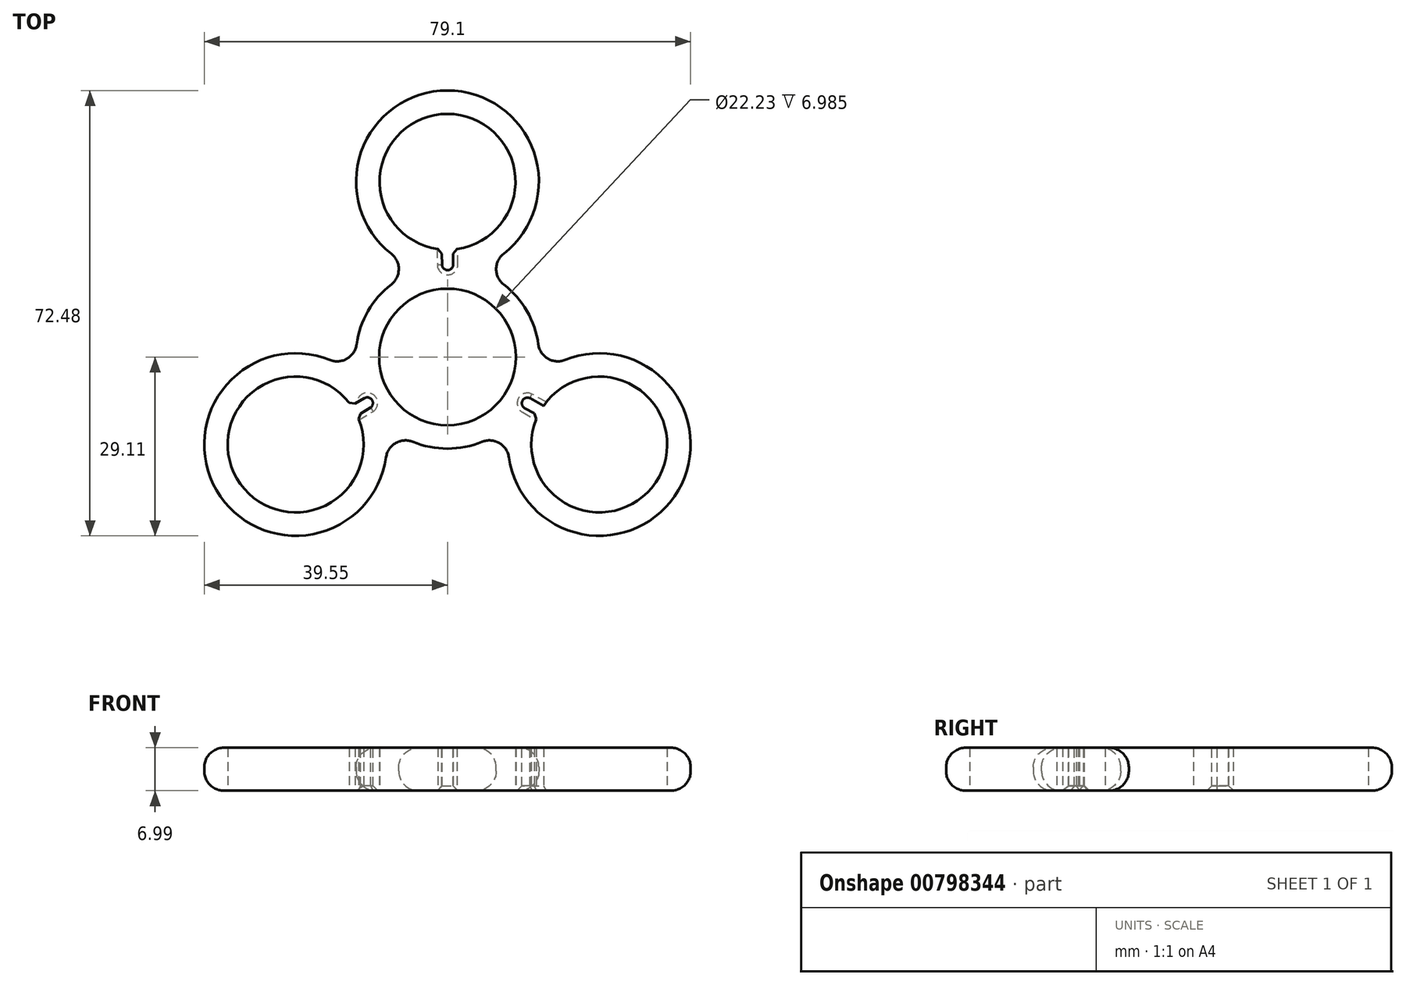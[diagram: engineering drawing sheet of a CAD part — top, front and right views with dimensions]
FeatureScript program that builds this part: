
annotation { "Feature Type Name" : "Feature", "Feature Type Description" : "" }
export const myFeature = defineFeature(function(context is Context, id is Id, definition is map)
    precondition{}
    {
        {
            var Q0;
            Q0=qCreatedBy(makeId("Top.planeOp"),FACE);
            var sketch = newSketch(context, id + "F0", { "sketchPlane" : qUnion([Q0])});
            skCircle(sketch, "E0", {"center": v(0, 0) * mm, "radius": 11.11 * mm});
            skCircle(sketch, "E1", {"center": v(0, 0) * mm, "radius": 14.92 * mm});
            skCircle(sketch, "E2", {"center": v(0, 28.51) * mm, "radius": 11.05 * mm});
            skCircle(sketch, "E3.0", {"center": v(0, 28.51) * mm, "radius": 14.86 * mm});
            skLineSegment(sketch, "E4", {"start": v(-5.64, 14.77) * mm, "end": v(-5.64, 13.81) * mm});
            skLineSegment(sketch, "E5.MirrorCS", {"start": v(5.64, 14.77) * mm, "end": v(5.64, 13.81) * mm});
            skCircle(sketch, "E6.1.0", {"center": v(-24.7, -14.26) * mm, "radius": 11.05 * mm});
            skCircle(sketch, "E6.1.1", {"center": v(-24.7, -14.26) * mm, "radius": 14.86 * mm});
            skLineSegment(sketch, "E6.1.2", {"start": v(-15.6, -2.5) * mm, "end": v(-14.79, -2.02) * mm});
            skLineSegment(sketch, "E6.1.3", {"start": v(-9.97, -12.27) * mm, "end": v(-9.14, -11.8) * mm});
            skCircle(sketch, "E6.2.0", {"center": v(24.7, -14.26) * mm, "radius": 11.05 * mm});
            skCircle(sketch, "E6.2.1", {"center": v(24.7, -14.26) * mm, "radius": 14.86 * mm});
            skLineSegment(sketch, "E6.2.2", {"start": v(9.97, -12.27) * mm, "end": v(9.14, -11.8) * mm});
            skLineSegment(sketch, "E6.2.3", {"start": v(15.6, -2.5) * mm, "end": v(14.79, -2.02) * mm});
            skLineSegment(sketch, "E7", {"start": v(0, 0) * mm, "end": v(0, 28.51) * mm, "construction": true});
            skSolve(sketch);
        }
        {
            var Q0;
            Q0=makeQuery(id+"F0.imprint","IMPRINT",FACE,{"disambiguationData":[TD([[makeQuery(id+"F0.imprint","IMPRINT",EDGE,{"derivedFrom":sQuery(id+"F0.wireOp",EDGE,"E0")}),-1.0]])]});
            extrude(context, id + "F1", {"entities" : qUnion([Q0]), "depth" : 7 * mm, "offsetDistance" : 25.4 * mm});
        }
        {
            var Q0;
            Q0=makeQuery(id+"F0.imprint","IMPRINT",FACE,{"disambiguationData":[TD([[makeQuery(id+"F0.imprint","IMPRINT",EDGE,{"derivedFrom":sQuery(id+"F0.wireOp",EDGE,"E6.2.0")}),-1.0]])]});
            var Q1;
            {var subQ0=sQuery(id+"F0.wireOp",EDGE,"E5.MirrorCS");Q1=makeQuery(id+"F0.imprint","IMPRINT",FACE,{"disambiguationData":[TD([[makeQuery(id+"F0.imprint","IMPRINT",EDGE,{"derivedFrom":subQ0}),1.0]])]});}
            var Q2;
            Q2=makeQuery(id+"F0.imprint","IMPRINT",FACE,{"disambiguationData":[TD([[makeQuery(id+"F0.imprint","IMPRINT",EDGE,{"derivedFrom":sQuery(id+"F0.wireOp",EDGE,"E2")}),-1.0]])]});
            var Q3;
            {var subQ0=sQuery(id+"F0.wireOp",EDGE,"E4");Q3=makeQuery(id+"F0.imprint","IMPRINT",FACE,{"disambiguationData":[TD([[makeQuery(id+"F0.imprint","IMPRINT",EDGE,{"derivedFrom":subQ0}),-1.0]])]});}
            var Q4;
            {var subQ0=sQuery(id+"F0.wireOp",EDGE,"E6.2.3");Q4=makeQuery(id+"F0.imprint","IMPRINT",FACE,{"disambiguationData":[TD([[makeQuery(id+"F0.imprint","IMPRINT",EDGE,{"derivedFrom":subQ0}),-1.0]])]});}
            var Q5;
            {var subQ0=sQuery(id+"F0.wireOp",EDGE,"E6.2.2");Q5=makeQuery(id+"F0.imprint","IMPRINT",FACE,{"disambiguationData":[TD([[makeQuery(id+"F0.imprint","IMPRINT",EDGE,{"derivedFrom":subQ0}),1.0]])]});}
            var Q6;
            Q6=makeQuery(id+"F0.imprint","IMPRINT",FACE,{"disambiguationData":[TD([[makeQuery(id+"F0.imprint","IMPRINT",EDGE,{"derivedFrom":sQuery(id+"F0.wireOp",EDGE,"E6.1.0")}),-1.0]])]});
            var Q7;
            {var subQ0=sQuery(id+"F0.wireOp",EDGE,"E6.1.3");Q7=makeQuery(id+"F0.imprint","IMPRINT",FACE,{"disambiguationData":[TD([[makeQuery(id+"F0.imprint","IMPRINT",EDGE,{"derivedFrom":subQ0}),-1.0]])]});}
            var Q8;
            Q8=makeQuery(id+"F0.imprint","IMPRINT",FACE,{"disambiguationData":[TD([[makeQuery(id+"F0.imprint","IMPRINT",EDGE,{"derivedFrom":sQuery(id+"F0.wireOp",EDGE,"E0")}),-1.0]])]});
            var Q9;
            {var subQ0=sQuery(id+"F0.wireOp",EDGE,"E6.1.2");Q9=makeQuery(id+"F0.imprint","IMPRINT",FACE,{"disambiguationData":[TD([[makeQuery(id+"F0.imprint","IMPRINT",EDGE,{"derivedFrom":subQ0}),1.0]])]});}
            var Q10;
            {var subQ0=sQuery(id+"F0.wireOp",EDGE,"E3.0");var subQ1=sQuery(id+"F0.wireOp",EDGE,"E1");var subQ2=makeQuery(id+"F0.imprint","INTERSECT",VERTEX,{"disambiguationData":[OD(0.0)],"derivedFrom":[subQ1,subQ0]});Q10=makeQuery(id+"F0.imprint","IMPRINT",FACE,{"disambiguationData":[TD([[makeQuery(id+"F0.imprint","IMPRINT",EDGE,{"disambiguationData":[TD([[subQ2,-1.0]])],"derivedFrom":subQ1}),1.0]])]});}
            var Q11;
            {var subQ0=sQuery(id+"F0.wireOp",EDGE,"E6.2.1");var subQ1=sQuery(id+"F0.wireOp",EDGE,"E1");var subQ2=makeQuery(id+"F0.imprint","INTERSECT",VERTEX,{"disambiguationData":[OD(0.0)],"derivedFrom":[subQ1,subQ0]});Q11=makeQuery(id+"F0.imprint","IMPRINT",FACE,{"disambiguationData":[TD([[makeQuery(id+"F0.imprint","IMPRINT",EDGE,{"disambiguationData":[TD([[subQ2,-1.0]])],"derivedFrom":subQ1}),1.0]])]});}
            var Q12;
            {var subQ0=sQuery(id+"F0.wireOp",EDGE,"E6.1.1");var subQ1=sQuery(id+"F0.wireOp",EDGE,"E1");var subQ2=makeQuery(id+"F0.imprint","INTERSECT",VERTEX,{"disambiguationData":[OD(0.0)],"derivedFrom":[subQ1,subQ0]});Q12=makeQuery(id+"F0.imprint","IMPRINT",FACE,{"disambiguationData":[TD([[makeQuery(id+"F0.imprint","IMPRINT",EDGE,{"disambiguationData":[TD([[subQ2,-1.0]])],"derivedFrom":subQ1}),1.0]])]});}
            extrude(context, id + "F2", {"entities" : qUnion([Q0, Q1, Q2, Q3, Q4, Q5, Q6, Q7, Q8, Q9, Q10, Q11, Q12]), "operationType" : NewBodyOperationType.ADD, "depth" : 7 * mm, "offsetDistance" : 25.4 * mm});
        }
        {
            var Q0;
            {var subQ0=sQuery(id+"F0.wireOp",EDGE,"E3.0");var subQ1=sQuery(id+"F0.wireOp",EDGE,"E1");var subQ2=makeQuery(id+"F0.imprint","INTERSECT",VERTEX,{"disambiguationData":[OD(1.0)],"derivedFrom":[subQ1,subQ0]});Q0=makeQuery(id+"F2.boolean.opBoolean","MERGE",EDGE,{"derivedFrom":[makeQuery(id+"F1.opExtrude","SWEPT_EDGE",EDGE,{"disambiguationData":[OSD([subQ1,subQ0]),TDD([subQ2])]}),makeQuery(id+"F2.opExtrude","SWEPT_EDGE",EDGE,{"disambiguationData":[OSD([subQ1,subQ0]),TDD([subQ2])]})]});}
            var Q1;
            {var subQ0=sQuery(id+"F0.wireOp",EDGE,"E3.0");var subQ1=sQuery(id+"F0.wireOp",EDGE,"E1");var subQ2=makeQuery(id+"F0.imprint","INTERSECT",VERTEX,{"disambiguationData":[OD(0.0)],"derivedFrom":[subQ1,subQ0]});Q1=makeQuery(id+"F2.boolean.opBoolean","MERGE",EDGE,{"derivedFrom":[makeQuery(id+"F1.opExtrude","SWEPT_EDGE",EDGE,{"disambiguationData":[OSD([subQ1,subQ0]),TDD([subQ2])]}),makeQuery(id+"F2.opExtrude","SWEPT_EDGE",EDGE,{"disambiguationData":[OSD([subQ1,subQ0]),TDD([subQ2])]})]});}
            var Q2;
            {var subQ0=sQuery(id+"F0.wireOp",EDGE,"E6.2.1");var subQ1=sQuery(id+"F0.wireOp",EDGE,"E1");var subQ2=makeQuery(id+"F0.imprint","INTERSECT",VERTEX,{"disambiguationData":[OD(1.0)],"derivedFrom":[subQ1,subQ0]});Q2=makeQuery(id+"F2.boolean.opBoolean","MERGE",EDGE,{"derivedFrom":[makeQuery(id+"F1.opExtrude","SWEPT_EDGE",EDGE,{"disambiguationData":[OSD([subQ1,subQ0]),TDD([subQ2])]}),makeQuery(id+"F2.opExtrude","SWEPT_EDGE",EDGE,{"disambiguationData":[OSD([subQ1,subQ0]),TDD([subQ2])]})]});}
            var Q3;
            {var subQ0=sQuery(id+"F0.wireOp",EDGE,"E6.2.1");var subQ1=sQuery(id+"F0.wireOp",EDGE,"E1");var subQ2=makeQuery(id+"F0.imprint","INTERSECT",VERTEX,{"disambiguationData":[OD(0.0)],"derivedFrom":[subQ1,subQ0]});Q3=makeQuery(id+"F2.boolean.opBoolean","MERGE",EDGE,{"derivedFrom":[makeQuery(id+"F1.opExtrude","SWEPT_EDGE",EDGE,{"disambiguationData":[OSD([subQ1,subQ0]),TDD([subQ2])]}),makeQuery(id+"F2.opExtrude","SWEPT_EDGE",EDGE,{"disambiguationData":[OSD([subQ1,subQ0]),TDD([subQ2])]})]});}
            var Q4;
            {var subQ0=sQuery(id+"F0.wireOp",EDGE,"E6.1.1");var subQ1=sQuery(id+"F0.wireOp",EDGE,"E1");var subQ2=makeQuery(id+"F0.imprint","INTERSECT",VERTEX,{"disambiguationData":[OD(1.0)],"derivedFrom":[subQ1,subQ0]});Q4=makeQuery(id+"F2.boolean.opBoolean","MERGE",EDGE,{"derivedFrom":[makeQuery(id+"F1.opExtrude","SWEPT_EDGE",EDGE,{"disambiguationData":[OSD([subQ1,subQ0]),TDD([subQ2])]}),makeQuery(id+"F2.opExtrude","SWEPT_EDGE",EDGE,{"disambiguationData":[OSD([subQ1,subQ0]),TDD([subQ2])]})]});}
            var Q5;
            {var subQ0=sQuery(id+"F0.wireOp",EDGE,"E6.1.1");var subQ1=sQuery(id+"F0.wireOp",EDGE,"E1");var subQ2=makeQuery(id+"F0.imprint","INTERSECT",VERTEX,{"disambiguationData":[OD(0.0)],"derivedFrom":[subQ1,subQ0]});Q5=makeQuery(id+"F2.boolean.opBoolean","MERGE",EDGE,{"derivedFrom":[makeQuery(id+"F1.opExtrude","SWEPT_EDGE",EDGE,{"disambiguationData":[OSD([subQ1,subQ0]),TDD([subQ2])]}),makeQuery(id+"F2.opExtrude","SWEPT_EDGE",EDGE,{"disambiguationData":[OSD([subQ1,subQ0]),TDD([subQ2])]})]});}
            fillet(context, id + "F3", {"entities" : qUnion([Q0, Q1, Q2, Q3, Q4, Q5]), "radius" : 3.17 * mm, "tangentPropagation" : true, "allowEdgeOverflow" : false});
        }
        {
            var Q0;
            {var subQ0=sQuery(id+"F0.wireOp",EDGE,"E6.1.3");var subQ1=sQuery(id+"F0.wireOp",EDGE,"E1");Q0=makeQuery(id+"F2.boolean.opBoolean","SPLIT",EDGE,{"disambiguationData":[TD([makeQuery(id+"F2.opExtrude","SWEPT_FACE",FACE,{"disambiguationData":[OSD([subQ0])]})])],"derivedFrom":makeQuery(id+"F1.opExtrude","CAP_EDGE",EDGE,{"disambiguationData":[OSD([subQ1])],"isStart":false})});}
            var Q1;
            Q1=makeQuery(id+"F2.opExtrude","CAP_EDGE",EDGE,{"disambiguationData":[OSD([sQuery(id+"F0.wireOp",EDGE,"E3.0")])],"isStart":true});
            var Q2;
            Q2=makeQuery(id+"F2.opExtrude","CAP_EDGE",EDGE,{"disambiguationData":[OSD([sQuery(id+"F0.wireOp",EDGE,"E6.2.1")])],"isStart":false});
            var Q3;
            Q3=makeQuery(id+"F2.opExtrude","CAP_EDGE",EDGE,{"disambiguationData":[OSD([sQuery(id+"F0.wireOp",EDGE,"E6.2.1")])],"isStart":true});
            var Q4;
            {var subQ0=sQuery(id+"F0.wireOp",EDGE,"E1");var subQ1=makeQuery(id+"F0.imprint","INTERSECT",VERTEX,{"derivedFrom":[subQ0,sQuery(id+"F0.wireOp",EDGE,"E5.MirrorCS")]});var subQ2=makeQuery(id+"F0.imprint","INTERSECT",VERTEX,{"derivedFrom":[subQ0,sQuery(id+"F0.wireOp",EDGE,"E6.2.3")]});Q4=makeQuery(id+"F1.opExtrude","CAP_EDGE",EDGE,{"disambiguationData":[OSD([subQ0]),TDD([makeQuery(id+"F0.imprint","IMPRINT",EDGE,{"disambiguationData":[TD([[subQ1,-1.0]])],"derivedFrom":subQ0}),makeQuery(id+"F0.imprint","IMPRINT",EDGE,{"disambiguationData":[TD([[subQ2,1.0]])],"derivedFrom":subQ0}),makeQuery(id+"F0.imprint","IMPRINT",EDGE,{"disambiguationData":[TD([[subQ1,1.0]])],"derivedFrom":subQ0})])],"isStart":true});}
            var Q5;
            {var subQ0=sQuery(id+"F0.wireOp",EDGE,"E6.2.1");var subQ1=sQuery(id+"F0.wireOp",EDGE,"E6.1.1");var subQ2=sQuery(id+"F0.wireOp",EDGE,"E5.MirrorCS");var subQ3=sQuery(id+"F0.wireOp",EDGE,"E3.0");var subQ4=sQuery(id+"F0.wireOp",EDGE,"E1");var subQ5=sQuery(id+"F0.wireOp",EDGE,"E0");Q5=makeQuery(id+"F3.opFillet","BLEND_EDGE",EDGE,{"blendedFrom":[makeQuery(id+"F2.opExtrude","SWEPT_EDGE",EDGE,{"disambiguationData":[OSD([subQ4,subQ2])]}),makeQuery(id+"F2.boolean.opBoolean","MERGE",FACE,{"derivedFrom":[makeQuery(id+"F1.opExtrude","CAP_FACE",FACE,{"disambiguationData":[OSD([subQ5,subQ4,subQ3,subQ1,subQ0])],"isStart":true}),makeQuery(id+"F2.opExtrude","CAP_FACE",FACE,{"disambiguationData":[OSD([subQ5,subQ4,sQuery(id+"F0.wireOp",EDGE,"E2"),subQ3,sQuery(id+"F0.wireOp",EDGE,"E4"),subQ2,sQuery(id+"F0.wireOp",EDGE,"E6.1.0"),subQ1,sQuery(id+"F0.wireOp",EDGE,"E6.1.2"),sQuery(id+"F0.wireOp",EDGE,"E6.2.0"),subQ0,sQuery(id+"F0.wireOp",EDGE,"E6.2.2")])],"isStart":true})]})],"blendedInto":[makeQuery(id+"F2.boolean.opBoolean","MERGE",FACE,{"derivedFrom":[makeQuery(id+"F1.opExtrude","CAP_FACE",FACE,{"disambiguationData":[OSD([subQ5,subQ4,subQ3,subQ1,subQ0])],"isStart":true}),makeQuery(id+"F2.opExtrude","CAP_FACE",FACE,{"disambiguationData":[OSD([subQ5,subQ4,sQuery(id+"F0.wireOp",EDGE,"E2"),subQ3,sQuery(id+"F0.wireOp",EDGE,"E4"),subQ2,sQuery(id+"F0.wireOp",EDGE,"E6.1.0"),subQ1,sQuery(id+"F0.wireOp",EDGE,"E6.1.2"),sQuery(id+"F0.wireOp",EDGE,"E6.2.0"),subQ0,sQuery(id+"F0.wireOp",EDGE,"E6.2.2")])],"isStart":true})]})]});}
            var Q6;
            {var subQ0=sQuery(id+"F0.wireOp",EDGE,"E6.2.1");var subQ1=sQuery(id+"F0.wireOp",EDGE,"E6.1.1");var subQ2=sQuery(id+"F0.wireOp",EDGE,"E5.MirrorCS");var subQ3=sQuery(id+"F0.wireOp",EDGE,"E3.0");var subQ4=sQuery(id+"F0.wireOp",EDGE,"E1");var subQ5=sQuery(id+"F0.wireOp",EDGE,"E0");Q6=makeQuery(id+"F3.opFillet","BLEND_EDGE",EDGE,{"blendedFrom":[makeQuery(id+"F2.opExtrude","SWEPT_EDGE",EDGE,{"disambiguationData":[OSD([subQ3,subQ2])]}),makeQuery(id+"F2.boolean.opBoolean","MERGE",FACE,{"derivedFrom":[makeQuery(id+"F1.opExtrude","CAP_FACE",FACE,{"disambiguationData":[OSD([subQ5,subQ4,subQ3,subQ1,subQ0])],"isStart":true}),makeQuery(id+"F2.opExtrude","CAP_FACE",FACE,{"disambiguationData":[OSD([subQ5,subQ4,sQuery(id+"F0.wireOp",EDGE,"E2"),subQ3,sQuery(id+"F0.wireOp",EDGE,"E4"),subQ2,sQuery(id+"F0.wireOp",EDGE,"E6.1.0"),subQ1,sQuery(id+"F0.wireOp",EDGE,"E6.1.2"),sQuery(id+"F0.wireOp",EDGE,"E6.2.0"),subQ0,sQuery(id+"F0.wireOp",EDGE,"E6.2.2")])],"isStart":true})]})],"blendedInto":[makeQuery(id+"F2.boolean.opBoolean","MERGE",FACE,{"derivedFrom":[makeQuery(id+"F1.opExtrude","CAP_FACE",FACE,{"disambiguationData":[OSD([subQ5,subQ4,subQ3,subQ1,subQ0])],"isStart":true}),makeQuery(id+"F2.opExtrude","CAP_FACE",FACE,{"disambiguationData":[OSD([subQ5,subQ4,sQuery(id+"F0.wireOp",EDGE,"E2"),subQ3,sQuery(id+"F0.wireOp",EDGE,"E4"),subQ2,sQuery(id+"F0.wireOp",EDGE,"E6.1.0"),subQ1,sQuery(id+"F0.wireOp",EDGE,"E6.1.2"),sQuery(id+"F0.wireOp",EDGE,"E6.2.0"),subQ0,sQuery(id+"F0.wireOp",EDGE,"E6.2.2")])],"isStart":true})]})]});}
            var Q7;
            {var subQ0=sQuery(id+"F0.wireOp",EDGE,"E6.2.1");var subQ1=sQuery(id+"F0.wireOp",EDGE,"E6.1.1");var subQ2=sQuery(id+"F0.wireOp",EDGE,"E5.MirrorCS");var subQ3=sQuery(id+"F0.wireOp",EDGE,"E3.0");var subQ4=sQuery(id+"F0.wireOp",EDGE,"E1");var subQ5=sQuery(id+"F0.wireOp",EDGE,"E0");Q7=makeQuery(id+"F3.opFillet","BLEND_EDGE",EDGE,{"blendedFrom":[makeQuery(id+"F2.opExtrude","SWEPT_EDGE",EDGE,{"disambiguationData":[OSD([subQ4,subQ2])]}),makeQuery(id+"F2.boolean.opBoolean","MERGE",FACE,{"derivedFrom":[makeQuery(id+"F1.opExtrude","CAP_FACE",FACE,{"disambiguationData":[OSD([subQ5,subQ4,subQ3,subQ1,subQ0])],"isStart":false}),makeQuery(id+"F2.opExtrude","CAP_FACE",FACE,{"disambiguationData":[OSD([subQ5,subQ4,sQuery(id+"F0.wireOp",EDGE,"E2"),subQ3,sQuery(id+"F0.wireOp",EDGE,"E4"),subQ2,sQuery(id+"F0.wireOp",EDGE,"E6.1.0"),subQ1,sQuery(id+"F0.wireOp",EDGE,"E6.1.2"),sQuery(id+"F0.wireOp",EDGE,"E6.2.0"),subQ0,sQuery(id+"F0.wireOp",EDGE,"E6.2.2")])],"isStart":false})]})],"blendedInto":[makeQuery(id+"F2.boolean.opBoolean","MERGE",FACE,{"derivedFrom":[makeQuery(id+"F1.opExtrude","CAP_FACE",FACE,{"disambiguationData":[OSD([subQ5,subQ4,subQ3,subQ1,subQ0])],"isStart":false}),makeQuery(id+"F2.opExtrude","CAP_FACE",FACE,{"disambiguationData":[OSD([subQ5,subQ4,sQuery(id+"F0.wireOp",EDGE,"E2"),subQ3,sQuery(id+"F0.wireOp",EDGE,"E4"),subQ2,sQuery(id+"F0.wireOp",EDGE,"E6.1.0"),subQ1,sQuery(id+"F0.wireOp",EDGE,"E6.1.2"),sQuery(id+"F0.wireOp",EDGE,"E6.2.0"),subQ0,sQuery(id+"F0.wireOp",EDGE,"E6.2.2")])],"isStart":false})]})]});}
            var Q8;
            {var subQ0=sQuery(id+"F0.wireOp",EDGE,"E6.2.1");var subQ1=sQuery(id+"F0.wireOp",EDGE,"E6.1.1");var subQ2=sQuery(id+"F0.wireOp",EDGE,"E5.MirrorCS");var subQ3=sQuery(id+"F0.wireOp",EDGE,"E3.0");var subQ4=sQuery(id+"F0.wireOp",EDGE,"E1");var subQ5=sQuery(id+"F0.wireOp",EDGE,"E0");Q8=makeQuery(id+"F3.opFillet","BLEND_EDGE",EDGE,{"blendedFrom":[makeQuery(id+"F2.opExtrude","SWEPT_EDGE",EDGE,{"disambiguationData":[OSD([subQ3,subQ2])]}),makeQuery(id+"F2.boolean.opBoolean","MERGE",FACE,{"derivedFrom":[makeQuery(id+"F1.opExtrude","CAP_FACE",FACE,{"disambiguationData":[OSD([subQ5,subQ4,subQ3,subQ1,subQ0])],"isStart":false}),makeQuery(id+"F2.opExtrude","CAP_FACE",FACE,{"disambiguationData":[OSD([subQ5,subQ4,sQuery(id+"F0.wireOp",EDGE,"E2"),subQ3,sQuery(id+"F0.wireOp",EDGE,"E4"),subQ2,sQuery(id+"F0.wireOp",EDGE,"E6.1.0"),subQ1,sQuery(id+"F0.wireOp",EDGE,"E6.1.2"),sQuery(id+"F0.wireOp",EDGE,"E6.2.0"),subQ0,sQuery(id+"F0.wireOp",EDGE,"E6.2.2")])],"isStart":false})]})],"blendedInto":[makeQuery(id+"F2.boolean.opBoolean","MERGE",FACE,{"derivedFrom":[makeQuery(id+"F1.opExtrude","CAP_FACE",FACE,{"disambiguationData":[OSD([subQ5,subQ4,subQ3,subQ1,subQ0])],"isStart":false}),makeQuery(id+"F2.opExtrude","CAP_FACE",FACE,{"disambiguationData":[OSD([subQ5,subQ4,sQuery(id+"F0.wireOp",EDGE,"E2"),subQ3,sQuery(id+"F0.wireOp",EDGE,"E4"),subQ2,sQuery(id+"F0.wireOp",EDGE,"E6.1.0"),subQ1,sQuery(id+"F0.wireOp",EDGE,"E6.1.2"),sQuery(id+"F0.wireOp",EDGE,"E6.2.0"),subQ0,sQuery(id+"F0.wireOp",EDGE,"E6.2.2")])],"isStart":false})]})]});}
            var Q9;
            Q9=makeQuery(id+"F2.opExtrude","SWEPT_FACE",FACE,{"disambiguationData":[OSD([sQuery(id+"F0.wireOp",EDGE,"E3.0")])]});
            var Q10;
            {var subQ0=sQuery(id+"F0.wireOp",EDGE,"E6.2.2");var subQ1=sQuery(id+"F0.wireOp",EDGE,"E6.2.1");var subQ2=sQuery(id+"F0.wireOp",EDGE,"E6.1.1");var subQ3=sQuery(id+"F0.wireOp",EDGE,"E3.0");var subQ4=sQuery(id+"F0.wireOp",EDGE,"E1");var subQ5=sQuery(id+"F0.wireOp",EDGE,"E0");Q10=makeQuery(id+"F3.opFillet","BLEND_EDGE",EDGE,{"blendedFrom":[makeQuery(id+"F2.opExtrude","SWEPT_EDGE",EDGE,{"disambiguationData":[OSD([subQ4,subQ0])]}),makeQuery(id+"F2.boolean.opBoolean","MERGE",FACE,{"derivedFrom":[makeQuery(id+"F1.opExtrude","CAP_FACE",FACE,{"disambiguationData":[OSD([subQ5,subQ4,subQ3,subQ2,subQ1])],"isStart":false}),makeQuery(id+"F2.opExtrude","CAP_FACE",FACE,{"disambiguationData":[OSD([subQ5,subQ4,sQuery(id+"F0.wireOp",EDGE,"E2"),subQ3,sQuery(id+"F0.wireOp",EDGE,"E4"),sQuery(id+"F0.wireOp",EDGE,"E5.MirrorCS"),sQuery(id+"F0.wireOp",EDGE,"E6.1.0"),subQ2,sQuery(id+"F0.wireOp",EDGE,"E6.1.2"),sQuery(id+"F0.wireOp",EDGE,"E6.2.0"),subQ1,subQ0])],"isStart":false})]})],"blendedInto":[makeQuery(id+"F2.boolean.opBoolean","MERGE",FACE,{"derivedFrom":[makeQuery(id+"F1.opExtrude","CAP_FACE",FACE,{"disambiguationData":[OSD([subQ5,subQ4,subQ3,subQ2,subQ1])],"isStart":false}),makeQuery(id+"F2.opExtrude","CAP_FACE",FACE,{"disambiguationData":[OSD([subQ5,subQ4,sQuery(id+"F0.wireOp",EDGE,"E2"),subQ3,sQuery(id+"F0.wireOp",EDGE,"E4"),sQuery(id+"F0.wireOp",EDGE,"E5.MirrorCS"),sQuery(id+"F0.wireOp",EDGE,"E6.1.0"),subQ2,sQuery(id+"F0.wireOp",EDGE,"E6.1.2"),sQuery(id+"F0.wireOp",EDGE,"E6.2.0"),subQ1,subQ0])],"isStart":false})]})]});}
            var Q11;
            {var subQ0=sQuery(id+"F0.wireOp",EDGE,"E6.2.2");var subQ1=sQuery(id+"F0.wireOp",EDGE,"E6.2.1");var subQ2=sQuery(id+"F0.wireOp",EDGE,"E6.1.1");var subQ3=sQuery(id+"F0.wireOp",EDGE,"E3.0");var subQ4=sQuery(id+"F0.wireOp",EDGE,"E1");var subQ5=sQuery(id+"F0.wireOp",EDGE,"E0");Q11=makeQuery(id+"F3.opFillet","BLEND_EDGE",EDGE,{"blendedFrom":[makeQuery(id+"F2.opExtrude","SWEPT_EDGE",EDGE,{"disambiguationData":[OSD([subQ1,subQ0])]}),makeQuery(id+"F2.boolean.opBoolean","MERGE",FACE,{"derivedFrom":[makeQuery(id+"F1.opExtrude","CAP_FACE",FACE,{"disambiguationData":[OSD([subQ5,subQ4,subQ3,subQ2,subQ1])],"isStart":false}),makeQuery(id+"F2.opExtrude","CAP_FACE",FACE,{"disambiguationData":[OSD([subQ5,subQ4,sQuery(id+"F0.wireOp",EDGE,"E2"),subQ3,sQuery(id+"F0.wireOp",EDGE,"E4"),sQuery(id+"F0.wireOp",EDGE,"E5.MirrorCS"),sQuery(id+"F0.wireOp",EDGE,"E6.1.0"),subQ2,sQuery(id+"F0.wireOp",EDGE,"E6.1.2"),sQuery(id+"F0.wireOp",EDGE,"E6.2.0"),subQ1,subQ0])],"isStart":false})]})],"blendedInto":[makeQuery(id+"F2.boolean.opBoolean","MERGE",FACE,{"derivedFrom":[makeQuery(id+"F1.opExtrude","CAP_FACE",FACE,{"disambiguationData":[OSD([subQ5,subQ4,subQ3,subQ2,subQ1])],"isStart":false}),makeQuery(id+"F2.opExtrude","CAP_FACE",FACE,{"disambiguationData":[OSD([subQ5,subQ4,sQuery(id+"F0.wireOp",EDGE,"E2"),subQ3,sQuery(id+"F0.wireOp",EDGE,"E4"),sQuery(id+"F0.wireOp",EDGE,"E5.MirrorCS"),sQuery(id+"F0.wireOp",EDGE,"E6.1.0"),subQ2,sQuery(id+"F0.wireOp",EDGE,"E6.1.2"),sQuery(id+"F0.wireOp",EDGE,"E6.2.0"),subQ1,subQ0])],"isStart":false})]})]});}
            var Q12;
            {var subQ0=sQuery(id+"F0.wireOp",EDGE,"E6.2.1");var subQ1=sQuery(id+"F0.wireOp",EDGE,"E6.1.1");var subQ2=sQuery(id+"F0.wireOp",EDGE,"E3.0");var subQ3=sQuery(id+"F0.wireOp",EDGE,"E1");var subQ4=sQuery(id+"F0.wireOp",EDGE,"E0");Q12=makeQuery(id+"F3.opFillet","BLEND_EDGE",EDGE,{"blendedFrom":[makeQuery(id+"F2.boolean.opBoolean","MERGE",EDGE,{"derivedFrom":[makeQuery(id+"F1.opExtrude","SWEPT_EDGE",EDGE,{"disambiguationData":[OSD([subQ3,subQ0]),TDD([makeQuery(id+"F0.imprint","INTERSECT",VERTEX,{"disambiguationData":[OD(1.0)],"derivedFrom":[subQ3,subQ0]})])]}),makeQuery(id+"F2.opExtrude","SWEPT_EDGE",EDGE,{"disambiguationData":[OSD([subQ3,subQ0])]})]}),makeQuery(id+"F2.boolean.opBoolean","MERGE",FACE,{"derivedFrom":[makeQuery(id+"F1.opExtrude","CAP_FACE",FACE,{"disambiguationData":[OSD([subQ4,subQ3,subQ2,subQ1,subQ0])],"isStart":false}),makeQuery(id+"F2.opExtrude","CAP_FACE",FACE,{"disambiguationData":[OSD([subQ4,subQ3,sQuery(id+"F0.wireOp",EDGE,"E2"),subQ2,sQuery(id+"F0.wireOp",EDGE,"E4"),sQuery(id+"F0.wireOp",EDGE,"E5.MirrorCS"),sQuery(id+"F0.wireOp",EDGE,"E6.1.0"),subQ1,sQuery(id+"F0.wireOp",EDGE,"E6.1.2"),sQuery(id+"F0.wireOp",EDGE,"E6.2.0"),subQ0,sQuery(id+"F0.wireOp",EDGE,"E6.2.2")])],"isStart":false})]})],"blendedInto":[makeQuery(id+"F2.boolean.opBoolean","MERGE",FACE,{"derivedFrom":[makeQuery(id+"F1.opExtrude","CAP_FACE",FACE,{"disambiguationData":[OSD([subQ4,subQ3,subQ2,subQ1,subQ0])],"isStart":false}),makeQuery(id+"F2.opExtrude","CAP_FACE",FACE,{"disambiguationData":[OSD([subQ4,subQ3,sQuery(id+"F0.wireOp",EDGE,"E2"),subQ2,sQuery(id+"F0.wireOp",EDGE,"E4"),sQuery(id+"F0.wireOp",EDGE,"E5.MirrorCS"),sQuery(id+"F0.wireOp",EDGE,"E6.1.0"),subQ1,sQuery(id+"F0.wireOp",EDGE,"E6.1.2"),sQuery(id+"F0.wireOp",EDGE,"E6.2.0"),subQ0,sQuery(id+"F0.wireOp",EDGE,"E6.2.2")])],"isStart":false})]})]});}
            var Q13;
            {var subQ0=sQuery(id+"F0.wireOp",EDGE,"E6.2.1");var subQ1=sQuery(id+"F0.wireOp",EDGE,"E6.1.1");var subQ2=sQuery(id+"F0.wireOp",EDGE,"E3.0");var subQ3=sQuery(id+"F0.wireOp",EDGE,"E1");var subQ4=sQuery(id+"F0.wireOp",EDGE,"E0");Q13=makeQuery(id+"F3.opFillet","BLEND_EDGE",EDGE,{"blendedFrom":[makeQuery(id+"F2.boolean.opBoolean","MERGE",EDGE,{"derivedFrom":[makeQuery(id+"F1.opExtrude","SWEPT_EDGE",EDGE,{"disambiguationData":[OSD([subQ3,subQ1]),TDD([makeQuery(id+"F0.imprint","INTERSECT",VERTEX,{"disambiguationData":[OD(1.0)],"derivedFrom":[subQ3,subQ1]})])]}),makeQuery(id+"F2.opExtrude","SWEPT_EDGE",EDGE,{"disambiguationData":[OSD([subQ3,subQ1])]})]}),makeQuery(id+"F2.boolean.opBoolean","MERGE",FACE,{"derivedFrom":[makeQuery(id+"F1.opExtrude","CAP_FACE",FACE,{"disambiguationData":[OSD([subQ4,subQ3,subQ2,subQ1,subQ0])],"isStart":false}),makeQuery(id+"F2.opExtrude","CAP_FACE",FACE,{"disambiguationData":[OSD([subQ4,subQ3,sQuery(id+"F0.wireOp",EDGE,"E2"),subQ2,sQuery(id+"F0.wireOp",EDGE,"E4"),sQuery(id+"F0.wireOp",EDGE,"E5.MirrorCS"),sQuery(id+"F0.wireOp",EDGE,"E6.1.0"),subQ1,sQuery(id+"F0.wireOp",EDGE,"E6.1.2"),sQuery(id+"F0.wireOp",EDGE,"E6.2.0"),subQ0,sQuery(id+"F0.wireOp",EDGE,"E6.2.2")])],"isStart":false})]})],"blendedInto":[makeQuery(id+"F2.boolean.opBoolean","MERGE",FACE,{"derivedFrom":[makeQuery(id+"F1.opExtrude","CAP_FACE",FACE,{"disambiguationData":[OSD([subQ4,subQ3,subQ2,subQ1,subQ0])],"isStart":false}),makeQuery(id+"F2.opExtrude","CAP_FACE",FACE,{"disambiguationData":[OSD([subQ4,subQ3,sQuery(id+"F0.wireOp",EDGE,"E2"),subQ2,sQuery(id+"F0.wireOp",EDGE,"E4"),sQuery(id+"F0.wireOp",EDGE,"E5.MirrorCS"),sQuery(id+"F0.wireOp",EDGE,"E6.1.0"),subQ1,sQuery(id+"F0.wireOp",EDGE,"E6.1.2"),sQuery(id+"F0.wireOp",EDGE,"E6.2.0"),subQ0,sQuery(id+"F0.wireOp",EDGE,"E6.2.2")])],"isStart":false})]})]});}
            var Q14;
            Q14=makeQuery(id+"F2.opExtrude","CAP_EDGE",EDGE,{"disambiguationData":[OSD([sQuery(id+"F0.wireOp",EDGE,"E6.1.1")])],"isStart":false});
            var Q15;
            {var subQ0=sQuery(id+"F0.wireOp",EDGE,"E6.2.1");var subQ1=sQuery(id+"F0.wireOp",EDGE,"E6.1.2");var subQ2=sQuery(id+"F0.wireOp",EDGE,"E6.1.1");var subQ3=sQuery(id+"F0.wireOp",EDGE,"E3.0");var subQ4=sQuery(id+"F0.wireOp",EDGE,"E1");var subQ5=sQuery(id+"F0.wireOp",EDGE,"E0");Q15=makeQuery(id+"F3.opFillet","BLEND_EDGE",EDGE,{"blendedFrom":[makeQuery(id+"F2.opExtrude","SWEPT_EDGE",EDGE,{"disambiguationData":[OSD([subQ4,subQ1])]}),makeQuery(id+"F2.boolean.opBoolean","MERGE",FACE,{"derivedFrom":[makeQuery(id+"F1.opExtrude","CAP_FACE",FACE,{"disambiguationData":[OSD([subQ5,subQ4,subQ3,subQ2,subQ0])],"isStart":false}),makeQuery(id+"F2.opExtrude","CAP_FACE",FACE,{"disambiguationData":[OSD([subQ5,subQ4,sQuery(id+"F0.wireOp",EDGE,"E2"),subQ3,sQuery(id+"F0.wireOp",EDGE,"E4"),sQuery(id+"F0.wireOp",EDGE,"E5.MirrorCS"),sQuery(id+"F0.wireOp",EDGE,"E6.1.0"),subQ2,subQ1,sQuery(id+"F0.wireOp",EDGE,"E6.2.0"),subQ0,sQuery(id+"F0.wireOp",EDGE,"E6.2.2")])],"isStart":false})]})],"blendedInto":[makeQuery(id+"F2.boolean.opBoolean","MERGE",FACE,{"derivedFrom":[makeQuery(id+"F1.opExtrude","CAP_FACE",FACE,{"disambiguationData":[OSD([subQ5,subQ4,subQ3,subQ2,subQ0])],"isStart":false}),makeQuery(id+"F2.opExtrude","CAP_FACE",FACE,{"disambiguationData":[OSD([subQ5,subQ4,sQuery(id+"F0.wireOp",EDGE,"E2"),subQ3,sQuery(id+"F0.wireOp",EDGE,"E4"),sQuery(id+"F0.wireOp",EDGE,"E5.MirrorCS"),sQuery(id+"F0.wireOp",EDGE,"E6.1.0"),subQ2,subQ1,sQuery(id+"F0.wireOp",EDGE,"E6.2.0"),subQ0,sQuery(id+"F0.wireOp",EDGE,"E6.2.2")])],"isStart":false})]})]});}
            var Q16;
            {var subQ0=sQuery(id+"F0.wireOp",EDGE,"E6.2.1");var subQ1=sQuery(id+"F0.wireOp",EDGE,"E6.1.2");var subQ2=sQuery(id+"F0.wireOp",EDGE,"E6.1.1");var subQ3=sQuery(id+"F0.wireOp",EDGE,"E3.0");var subQ4=sQuery(id+"F0.wireOp",EDGE,"E1");var subQ5=sQuery(id+"F0.wireOp",EDGE,"E0");Q16=makeQuery(id+"F3.opFillet","BLEND_EDGE",EDGE,{"blendedFrom":[makeQuery(id+"F2.opExtrude","SWEPT_EDGE",EDGE,{"disambiguationData":[OSD([subQ2,subQ1])]}),makeQuery(id+"F2.boolean.opBoolean","MERGE",FACE,{"derivedFrom":[makeQuery(id+"F1.opExtrude","CAP_FACE",FACE,{"disambiguationData":[OSD([subQ5,subQ4,subQ3,subQ2,subQ0])],"isStart":false}),makeQuery(id+"F2.opExtrude","CAP_FACE",FACE,{"disambiguationData":[OSD([subQ5,subQ4,sQuery(id+"F0.wireOp",EDGE,"E2"),subQ3,sQuery(id+"F0.wireOp",EDGE,"E4"),sQuery(id+"F0.wireOp",EDGE,"E5.MirrorCS"),sQuery(id+"F0.wireOp",EDGE,"E6.1.0"),subQ2,subQ1,sQuery(id+"F0.wireOp",EDGE,"E6.2.0"),subQ0,sQuery(id+"F0.wireOp",EDGE,"E6.2.2")])],"isStart":false})]})],"blendedInto":[makeQuery(id+"F2.boolean.opBoolean","MERGE",FACE,{"derivedFrom":[makeQuery(id+"F1.opExtrude","CAP_FACE",FACE,{"disambiguationData":[OSD([subQ5,subQ4,subQ3,subQ2,subQ0])],"isStart":false}),makeQuery(id+"F2.opExtrude","CAP_FACE",FACE,{"disambiguationData":[OSD([subQ5,subQ4,sQuery(id+"F0.wireOp",EDGE,"E2"),subQ3,sQuery(id+"F0.wireOp",EDGE,"E4"),sQuery(id+"F0.wireOp",EDGE,"E5.MirrorCS"),sQuery(id+"F0.wireOp",EDGE,"E6.1.0"),subQ2,subQ1,sQuery(id+"F0.wireOp",EDGE,"E6.2.0"),subQ0,sQuery(id+"F0.wireOp",EDGE,"E6.2.2")])],"isStart":false})]})]});}
            var Q17;
            {var subQ0=sQuery(id+"F0.wireOp",EDGE,"E6.2.1");var subQ1=sQuery(id+"F0.wireOp",EDGE,"E6.1.1");var subQ2=sQuery(id+"F0.wireOp",EDGE,"E4");var subQ3=sQuery(id+"F0.wireOp",EDGE,"E3.0");var subQ4=sQuery(id+"F0.wireOp",EDGE,"E1");var subQ5=sQuery(id+"F0.wireOp",EDGE,"E0");Q17=makeQuery(id+"F3.opFillet","BLEND_EDGE",EDGE,{"blendedFrom":[makeQuery(id+"F2.opExtrude","SWEPT_EDGE",EDGE,{"disambiguationData":[OSD([subQ3,subQ2])]}),makeQuery(id+"F2.boolean.opBoolean","MERGE",FACE,{"derivedFrom":[makeQuery(id+"F1.opExtrude","CAP_FACE",FACE,{"disambiguationData":[OSD([subQ5,subQ4,subQ3,subQ1,subQ0])],"isStart":false}),makeQuery(id+"F2.opExtrude","CAP_FACE",FACE,{"disambiguationData":[OSD([subQ5,subQ4,sQuery(id+"F0.wireOp",EDGE,"E2"),subQ3,subQ2,sQuery(id+"F0.wireOp",EDGE,"E5.MirrorCS"),sQuery(id+"F0.wireOp",EDGE,"E6.1.0"),subQ1,sQuery(id+"F0.wireOp",EDGE,"E6.1.2"),sQuery(id+"F0.wireOp",EDGE,"E6.2.0"),subQ0,sQuery(id+"F0.wireOp",EDGE,"E6.2.2")])],"isStart":false})]})],"blendedInto":[makeQuery(id+"F2.boolean.opBoolean","MERGE",FACE,{"derivedFrom":[makeQuery(id+"F1.opExtrude","CAP_FACE",FACE,{"disambiguationData":[OSD([subQ5,subQ4,subQ3,subQ1,subQ0])],"isStart":false}),makeQuery(id+"F2.opExtrude","CAP_FACE",FACE,{"disambiguationData":[OSD([subQ5,subQ4,sQuery(id+"F0.wireOp",EDGE,"E2"),subQ3,subQ2,sQuery(id+"F0.wireOp",EDGE,"E5.MirrorCS"),sQuery(id+"F0.wireOp",EDGE,"E6.1.0"),subQ1,sQuery(id+"F0.wireOp",EDGE,"E6.1.2"),sQuery(id+"F0.wireOp",EDGE,"E6.2.0"),subQ0,sQuery(id+"F0.wireOp",EDGE,"E6.2.2")])],"isStart":false})]})]});}
            var Q18;
            {var subQ0=sQuery(id+"F0.wireOp",EDGE,"E6.2.1");var subQ1=sQuery(id+"F0.wireOp",EDGE,"E6.1.1");var subQ2=sQuery(id+"F0.wireOp",EDGE,"E4");var subQ3=sQuery(id+"F0.wireOp",EDGE,"E3.0");var subQ4=sQuery(id+"F0.wireOp",EDGE,"E1");var subQ5=sQuery(id+"F0.wireOp",EDGE,"E0");Q18=makeQuery(id+"F3.opFillet","BLEND_EDGE",EDGE,{"blendedFrom":[makeQuery(id+"F2.opExtrude","SWEPT_EDGE",EDGE,{"disambiguationData":[OSD([subQ4,subQ2])]}),makeQuery(id+"F2.boolean.opBoolean","MERGE",FACE,{"derivedFrom":[makeQuery(id+"F1.opExtrude","CAP_FACE",FACE,{"disambiguationData":[OSD([subQ5,subQ4,subQ3,subQ1,subQ0])],"isStart":false}),makeQuery(id+"F2.opExtrude","CAP_FACE",FACE,{"disambiguationData":[OSD([subQ5,subQ4,sQuery(id+"F0.wireOp",EDGE,"E2"),subQ3,subQ2,sQuery(id+"F0.wireOp",EDGE,"E5.MirrorCS"),sQuery(id+"F0.wireOp",EDGE,"E6.1.0"),subQ1,sQuery(id+"F0.wireOp",EDGE,"E6.1.2"),sQuery(id+"F0.wireOp",EDGE,"E6.2.0"),subQ0,sQuery(id+"F0.wireOp",EDGE,"E6.2.2")])],"isStart":false})]})],"blendedInto":[makeQuery(id+"F2.boolean.opBoolean","MERGE",FACE,{"derivedFrom":[makeQuery(id+"F1.opExtrude","CAP_FACE",FACE,{"disambiguationData":[OSD([subQ5,subQ4,subQ3,subQ1,subQ0])],"isStart":false}),makeQuery(id+"F2.opExtrude","CAP_FACE",FACE,{"disambiguationData":[OSD([subQ5,subQ4,sQuery(id+"F0.wireOp",EDGE,"E2"),subQ3,subQ2,sQuery(id+"F0.wireOp",EDGE,"E5.MirrorCS"),sQuery(id+"F0.wireOp",EDGE,"E6.1.0"),subQ1,sQuery(id+"F0.wireOp",EDGE,"E6.1.2"),sQuery(id+"F0.wireOp",EDGE,"E6.2.0"),subQ0,sQuery(id+"F0.wireOp",EDGE,"E6.2.2")])],"isStart":false})]})]});}
            fillet(context, id + "F4", {"entities" : qUnion([Q0, Q1, Q2, Q3, Q4, Q5, Q6, Q7, Q8, Q9, Q10, Q11, Q12, Q13, Q14, Q15, Q16, Q17, Q18]), "radius" : 3.17 * mm, "tangentPropagation" : true, "allowEdgeOverflow" : false});
        }
        {
            var Q0;
            {var subQ0=sQuery(id+"F0.wireOp",EDGE,"E1");Q0=makeQuery(id+"F2.boolean.opBoolean","MERGE",FACE,{"derivedFrom":[makeQuery(id+"F1.opExtrude","CAP_FACE",FACE,{"disambiguationData":[OSD([sQuery(id+"F0.wireOp",EDGE,"E0"),subQ0])],"isStart":false}),makeQuery(id+"F2.opExtrude","CAP_FACE",FACE,{"disambiguationData":[OSD([subQ0,sQuery(id+"F0.wireOp",EDGE,"E2"),sQuery(id+"F0.wireOp",EDGE,"E3.0"),sQuery(id+"F0.wireOp",EDGE,"E4"),sQuery(id+"F0.wireOp",EDGE,"E5.MirrorCS")])],"isStart":false}),makeQuery(id+"F2.opExtrude","CAP_FACE",FACE,{"disambiguationData":[OSD([subQ0,sQuery(id+"F0.wireOp",EDGE,"E6.1.0"),sQuery(id+"F0.wireOp",EDGE,"E6.1.1"),sQuery(id+"F0.wireOp",EDGE,"E6.1.2"),sQuery(id+"F0.wireOp",EDGE,"E6.1.3")])],"isStart":false}),makeQuery(id+"F2.opExtrude","CAP_FACE",FACE,{"disambiguationData":[OSD([subQ0,sQuery(id+"F0.wireOp",EDGE,"E6.2.0"),sQuery(id+"F0.wireOp",EDGE,"E6.2.1"),sQuery(id+"F0.wireOp",EDGE,"E6.2.2"),sQuery(id+"F0.wireOp",EDGE,"E6.2.3")])],"isStart":false})]});}
            var sketch = newSketch(context, id + "F5", { "sketchPlane" : qUnion([Q0])});
            skLineSegment(sketch, "E8.left", {"start": v(0.94, 15.05) * mm, "end": v(0.89, 19.22) * mm});
            skLineSegment(sketch, "E8.right", {"start": v(-0.89, 14.96) * mm, "end": v(-0.94, 19.13) * mm});
            skPoint(sketch, "E8.middle", {"position": v(0, 17.09) * mm});
            skArc(sketch, "E9", {"start": v(0.89, 19.22) * mm, "mid": v(-0.07, 20.12) * mm, "end": v(-0.94, 19.13) * mm});
            skArc(sketch, "E10", {"start": v(0.94, 15.05) * mm, "mid": v(0.07, 14.12) * mm, "end": v(-0.89, 14.96) * mm});
            skLineSegment(sketch, "E11.1.0", {"start": v(-13.5, -6.71) * mm, "end": v(-17.09, -8.84) * mm});
            skArc(sketch, "E11.1.1", {"start": v(-17.09, -8.84) * mm, "mid": v(-17.4, -10.12) * mm, "end": v(-16.1, -10.38) * mm});
            skLineSegment(sketch, "E11.1.2", {"start": v(-12.5, -8.25) * mm, "end": v(-16.1, -10.38) * mm});
            skArc(sketch, "E11.1.3", {"start": v(-13.5, -6.71) * mm, "mid": v(-12.27, -7) * mm, "end": v(-12.5, -8.25) * mm});
            skLineSegment(sketch, "E11.2.0", {"start": v(12.56, -8.34) * mm, "end": v(16.2, -10.38) * mm});
            skArc(sketch, "E11.2.1", {"start": v(16.2, -10.38) * mm, "mid": v(17.46, -10) * mm, "end": v(17.04, -8.75) * mm});
            skLineSegment(sketch, "E11.2.2", {"start": v(13.4, -6.71) * mm, "end": v(17.04, -8.75) * mm});
            skArc(sketch, "E11.2.3", {"start": v(12.56, -8.34) * mm, "mid": v(12.2, -7.13) * mm, "end": v(13.4, -6.71) * mm});
            skPoint(sketch, "E11.center", {"position": v(0, 0) * mm});
            skSolve(sketch);
        }
        {
            var Q0;
            Q0=makeQuery(id+"F5.imprint","IMPRINT",FACE,{"disambiguationData":[TD([[makeQuery(id+"F5.imprint","IMPRINT",EDGE,{"derivedFrom":sQuery(id+"F5.wireOp",EDGE,"E8.left")}),1.0]])]});
            var Q1;
            Q1=makeQuery(id+"F5.imprint","IMPRINT",FACE,{"disambiguationData":[TD([[makeQuery(id+"F5.imprint","IMPRINT",EDGE,{"derivedFrom":sQuery(id+"F5.wireOp",EDGE,"E11.1.0")}),1.0]])]});
            var Q2;
            Q2=makeQuery(id+"F5.imprint","IMPRINT",FACE,{"disambiguationData":[TD([[makeQuery(id+"F5.imprint","IMPRINT",EDGE,{"derivedFrom":sQuery(id+"F5.wireOp",EDGE,"E11.2.0")}),1.0]])]});
            extrude(context, id + "F6", {"entities" : qUnion([Q0, Q1, Q2]), "operationType" : NewBodyOperationType.REMOVE, "endBound" : BoundingType.THROUGH_ALL, "oppositeDirection" : true, "depth" : 25.4 * mm, "offsetDistance" : 25.4 * mm});
        }
        {
            var Q0;
            Q0=makeQuery(id+"F6.boolean.opBoolean","COPY",EDGE,{"derivedFrom":makeQuery(id+"F6.opExtrude","CAP_EDGE",EDGE,{"disambiguationData":[OSD([sQuery(id+"F5.wireOp",EDGE,"E11.1.2")])],"isStart":true})});
            var Q1;
            Q1=makeQuery(id+"F6.boolean.opBoolean","COPY",EDGE,{"derivedFrom":makeQuery(id+"F6.opExtrude","CAP_EDGE",EDGE,{"disambiguationData":[OSD([sQuery(id+"F5.wireOp",EDGE,"E11.1.1")])],"isStart":true})});
            var Q2;
            Q2=makeQuery(id+"F6.boolean.opBoolean","COPY",EDGE,{"derivedFrom":makeQuery(id+"F6.opExtrude","CAP_EDGE",EDGE,{"disambiguationData":[OSD([sQuery(id+"F5.wireOp",EDGE,"E11.1.0")])],"isStart":true})});
            var Q3;
            Q3=makeQuery(id+"F6.boolean.opBoolean","COPY",EDGE,{"derivedFrom":makeQuery(id+"F6.opExtrude","CAP_EDGE",EDGE,{"disambiguationData":[OSD([sQuery(id+"F5.wireOp",EDGE,"E11.1.3")])],"isStart":true})});
            var Q4;
            Q4=makeQuery(id+"F6.boolean.opBoolean","COPY",EDGE,{"derivedFrom":makeQuery(id+"F6.opExtrude","CAP_EDGE",EDGE,{"disambiguationData":[OSD([sQuery(id+"F5.wireOp",EDGE,"E11.2.0")])],"isStart":true})});
            var Q5;
            Q5=makeQuery(id+"F6.boolean.opBoolean","COPY",EDGE,{"derivedFrom":makeQuery(id+"F6.opExtrude","CAP_EDGE",EDGE,{"disambiguationData":[OSD([sQuery(id+"F5.wireOp",EDGE,"E10")])],"isStart":true})});
            var Q6;
            {var subQ0=sQuery(id+"F0.wireOp",EDGE,"E1");Q6=makeQuery(id+"F6.boolean.opBoolean","INTERSECT",EDGE,{"derivedFrom":[makeQuery(id+"F2.boolean.opBoolean","MERGE",FACE,{"derivedFrom":[makeQuery(id+"F1.opExtrude","CAP_FACE",FACE,{"disambiguationData":[OSD([sQuery(id+"F0.wireOp",EDGE,"E0"),subQ0])],"isStart":true}),makeQuery(id+"F2.opExtrude","CAP_FACE",FACE,{"disambiguationData":[OSD([subQ0,sQuery(id+"F0.wireOp",EDGE,"E2"),sQuery(id+"F0.wireOp",EDGE,"E3.0"),sQuery(id+"F0.wireOp",EDGE,"E4"),sQuery(id+"F0.wireOp",EDGE,"E5.MirrorCS")])],"isStart":true}),makeQuery(id+"F2.opExtrude","CAP_FACE",FACE,{"disambiguationData":[OSD([subQ0,sQuery(id+"F0.wireOp",EDGE,"E6.1.0"),sQuery(id+"F0.wireOp",EDGE,"E6.1.1"),sQuery(id+"F0.wireOp",EDGE,"E6.1.2"),sQuery(id+"F0.wireOp",EDGE,"E6.1.3")])],"isStart":true}),makeQuery(id+"F2.opExtrude","CAP_FACE",FACE,{"disambiguationData":[OSD([subQ0,sQuery(id+"F0.wireOp",EDGE,"E6.2.0"),sQuery(id+"F0.wireOp",EDGE,"E6.2.1"),sQuery(id+"F0.wireOp",EDGE,"E6.2.2"),sQuery(id+"F0.wireOp",EDGE,"E6.2.3")])],"isStart":true})]}),makeQuery(id+"F6.opExtrude","SWEPT_FACE",FACE,{"disambiguationData":[OSD([sQuery(id+"F5.wireOp",EDGE,"E11.1.1")])]})]});}
            var Q7;
            {var subQ0=sQuery(id+"F0.wireOp",EDGE,"E1");Q7=makeQuery(id+"F6.boolean.opBoolean","INTERSECT",EDGE,{"derivedFrom":[makeQuery(id+"F2.boolean.opBoolean","MERGE",FACE,{"derivedFrom":[makeQuery(id+"F1.opExtrude","CAP_FACE",FACE,{"disambiguationData":[OSD([sQuery(id+"F0.wireOp",EDGE,"E0"),subQ0])],"isStart":true}),makeQuery(id+"F2.opExtrude","CAP_FACE",FACE,{"disambiguationData":[OSD([subQ0,sQuery(id+"F0.wireOp",EDGE,"E2"),sQuery(id+"F0.wireOp",EDGE,"E3.0"),sQuery(id+"F0.wireOp",EDGE,"E4"),sQuery(id+"F0.wireOp",EDGE,"E5.MirrorCS")])],"isStart":true}),makeQuery(id+"F2.opExtrude","CAP_FACE",FACE,{"disambiguationData":[OSD([subQ0,sQuery(id+"F0.wireOp",EDGE,"E6.1.0"),sQuery(id+"F0.wireOp",EDGE,"E6.1.1"),sQuery(id+"F0.wireOp",EDGE,"E6.1.2"),sQuery(id+"F0.wireOp",EDGE,"E6.1.3")])],"isStart":true}),makeQuery(id+"F2.opExtrude","CAP_FACE",FACE,{"disambiguationData":[OSD([subQ0,sQuery(id+"F0.wireOp",EDGE,"E6.2.0"),sQuery(id+"F0.wireOp",EDGE,"E6.2.1"),sQuery(id+"F0.wireOp",EDGE,"E6.2.2"),sQuery(id+"F0.wireOp",EDGE,"E6.2.3")])],"isStart":true})]}),makeQuery(id+"F6.opExtrude","SWEPT_FACE",FACE,{"disambiguationData":[OSD([sQuery(id+"F5.wireOp",EDGE,"E10")])]})]});}
            var Q8;
            {var subQ0=sQuery(id+"F0.wireOp",EDGE,"E1");Q8=makeQuery(id+"F6.boolean.opBoolean","INTERSECT",EDGE,{"derivedFrom":[makeQuery(id+"F2.boolean.opBoolean","MERGE",FACE,{"derivedFrom":[makeQuery(id+"F1.opExtrude","CAP_FACE",FACE,{"disambiguationData":[OSD([sQuery(id+"F0.wireOp",EDGE,"E0"),subQ0])],"isStart":true}),makeQuery(id+"F2.opExtrude","CAP_FACE",FACE,{"disambiguationData":[OSD([subQ0,sQuery(id+"F0.wireOp",EDGE,"E2"),sQuery(id+"F0.wireOp",EDGE,"E3.0"),sQuery(id+"F0.wireOp",EDGE,"E4"),sQuery(id+"F0.wireOp",EDGE,"E5.MirrorCS")])],"isStart":true}),makeQuery(id+"F2.opExtrude","CAP_FACE",FACE,{"disambiguationData":[OSD([subQ0,sQuery(id+"F0.wireOp",EDGE,"E6.1.0"),sQuery(id+"F0.wireOp",EDGE,"E6.1.1"),sQuery(id+"F0.wireOp",EDGE,"E6.1.2"),sQuery(id+"F0.wireOp",EDGE,"E6.1.3")])],"isStart":true}),makeQuery(id+"F2.opExtrude","CAP_FACE",FACE,{"disambiguationData":[OSD([subQ0,sQuery(id+"F0.wireOp",EDGE,"E6.2.0"),sQuery(id+"F0.wireOp",EDGE,"E6.2.1"),sQuery(id+"F0.wireOp",EDGE,"E6.2.2"),sQuery(id+"F0.wireOp",EDGE,"E6.2.3")])],"isStart":true})]}),makeQuery(id+"F6.opExtrude","SWEPT_FACE",FACE,{"disambiguationData":[OSD([sQuery(id+"F5.wireOp",EDGE,"E11.2.3")])]})]});}
            var Q9;
            {var subQ0=sQuery(id+"F0.wireOp",EDGE,"E6.2.1");var subQ1=sQuery(id+"F0.wireOp",EDGE,"E6.1.1");var subQ2=sQuery(id+"F0.wireOp",EDGE,"E3.0");var subQ3=sQuery(id+"F0.wireOp",EDGE,"E1");var subQ4=sQuery(id+"F0.wireOp",EDGE,"E0");Q9=makeQuery(id+"F6.boolean.opBoolean","INTERSECT",EDGE,{"derivedFrom":[makeQuery(id+"F2.boolean.opBoolean","MERGE",FACE,{"derivedFrom":[makeQuery(id+"F1.opExtrude","CAP_FACE",FACE,{"disambiguationData":[OSD([subQ4,subQ3,subQ2,subQ1,subQ0])],"isStart":true}),makeQuery(id+"F2.opExtrude","CAP_FACE",FACE,{"disambiguationData":[OSD([subQ4,subQ3,sQuery(id+"F0.wireOp",EDGE,"E2"),subQ2,sQuery(id+"F0.wireOp",EDGE,"E6.1.0"),subQ1,sQuery(id+"F0.wireOp",EDGE,"E6.2.0"),subQ0])],"isStart":true})]}),makeQuery(id+"F6.opExtrude","SWEPT_FACE",FACE,{"disambiguationData":[OSD([sQuery(id+"F5.wireOp",EDGE,"E11.2.2")])]})]});}
            var Q10;
            Q10=makeQuery(id+"F6.boolean.opBoolean","COPY",EDGE,{"derivedFrom":makeQuery(id+"F6.opExtrude","CAP_EDGE",EDGE,{"disambiguationData":[OSD([sQuery(id+"F5.wireOp",EDGE,"E11.2.2")])],"isStart":true})});
            var Q11;
            Q11=makeQuery(id+"F6.boolean.opBoolean","INTERSECT",EDGE,{"derivedFrom":[makeQuery(id+"F2.opExtrude","SWEPT_FACE",FACE,{"disambiguationData":[OSD([sQuery(id+"F0.wireOp",EDGE,"E6.2.0")])]}),makeQuery(id+"F6.opExtrude","SWEPT_FACE",FACE,{"disambiguationData":[OSD([sQuery(id+"F5.wireOp",EDGE,"E11.2.0")])]})]});
            var Q12;
            Q12=makeQuery(id+"F6.boolean.opBoolean","INTERSECT",EDGE,{"derivedFrom":[makeQuery(id+"F2.opExtrude","SWEPT_FACE",FACE,{"disambiguationData":[OSD([sQuery(id+"F0.wireOp",EDGE,"E6.2.0")])]}),makeQuery(id+"F6.opExtrude","SWEPT_FACE",FACE,{"disambiguationData":[OSD([sQuery(id+"F5.wireOp",EDGE,"E11.2.1")])]})]});
            var Q13;
            Q13=makeQuery(id+"F6.boolean.opBoolean","COPY",EDGE,{"derivedFrom":makeQuery(id+"F6.opExtrude","CAP_EDGE",EDGE,{"disambiguationData":[OSD([sQuery(id+"F5.wireOp",EDGE,"E8.right")])],"isStart":true})});
            var Q14;
            Q14=makeQuery(id+"F6.boolean.opBoolean","INTERSECT",EDGE,{"derivedFrom":[makeQuery(id+"F2.opExtrude","SWEPT_FACE",FACE,{"disambiguationData":[OSD([sQuery(id+"F0.wireOp",EDGE,"E2")])]}),makeQuery(id+"F6.opExtrude","SWEPT_FACE",FACE,{"disambiguationData":[OSD([sQuery(id+"F5.wireOp",EDGE,"E8.right")])]})]});
            var Q15;
            Q15=makeQuery(id+"F6.boolean.opBoolean","INTERSECT",EDGE,{"derivedFrom":[makeQuery(id+"F2.opExtrude","SWEPT_FACE",FACE,{"disambiguationData":[OSD([sQuery(id+"F0.wireOp",EDGE,"E2")])]}),makeQuery(id+"F6.opExtrude","SWEPT_FACE",FACE,{"disambiguationData":[OSD([sQuery(id+"F5.wireOp",EDGE,"E8.left")])]})]});
            var Q16;
            {var subQ0=sQuery(id+"F0.wireOp",EDGE,"E6.2.1");var subQ1=sQuery(id+"F0.wireOp",EDGE,"E6.1.1");var subQ2=sQuery(id+"F0.wireOp",EDGE,"E3.0");var subQ3=sQuery(id+"F0.wireOp",EDGE,"E1");var subQ4=sQuery(id+"F0.wireOp",EDGE,"E0");Q16=makeQuery(id+"F6.boolean.opBoolean","INTERSECT",EDGE,{"derivedFrom":[makeQuery(id+"F2.boolean.opBoolean","MERGE",FACE,{"derivedFrom":[makeQuery(id+"F1.opExtrude","CAP_FACE",FACE,{"disambiguationData":[OSD([subQ4,subQ3,subQ2,subQ1,subQ0])],"isStart":true}),makeQuery(id+"F2.opExtrude","CAP_FACE",FACE,{"disambiguationData":[OSD([subQ4,subQ3,sQuery(id+"F0.wireOp",EDGE,"E2"),subQ2,sQuery(id+"F0.wireOp",EDGE,"E6.1.0"),subQ1,sQuery(id+"F0.wireOp",EDGE,"E6.2.0"),subQ0])],"isStart":true})]}),makeQuery(id+"F6.opExtrude","SWEPT_FACE",FACE,{"disambiguationData":[OSD([sQuery(id+"F5.wireOp",EDGE,"E8.right")])]})]});}
            var Q17;
            {var subQ0=sQuery(id+"F0.wireOp",EDGE,"E6.2.1");var subQ1=sQuery(id+"F0.wireOp",EDGE,"E6.1.1");var subQ2=sQuery(id+"F0.wireOp",EDGE,"E3.0");var subQ3=sQuery(id+"F0.wireOp",EDGE,"E1");var subQ4=sQuery(id+"F0.wireOp",EDGE,"E0");Q17=makeQuery(id+"F6.boolean.opBoolean","INTERSECT",EDGE,{"derivedFrom":[makeQuery(id+"F2.boolean.opBoolean","MERGE",FACE,{"derivedFrom":[makeQuery(id+"F1.opExtrude","CAP_FACE",FACE,{"disambiguationData":[OSD([subQ4,subQ3,subQ2,subQ1,subQ0])],"isStart":true}),makeQuery(id+"F2.opExtrude","CAP_FACE",FACE,{"disambiguationData":[OSD([subQ4,subQ3,sQuery(id+"F0.wireOp",EDGE,"E2"),subQ2,sQuery(id+"F0.wireOp",EDGE,"E6.1.0"),subQ1,sQuery(id+"F0.wireOp",EDGE,"E6.2.0"),subQ0])],"isStart":true})]}),makeQuery(id+"F6.opExtrude","SWEPT_FACE",FACE,{"disambiguationData":[OSD([sQuery(id+"F5.wireOp",EDGE,"E11.1.2")])]})]});}
            var Q18;
            Q18=makeQuery(id+"F6.boolean.opBoolean","INTERSECT",EDGE,{"derivedFrom":[makeQuery(id+"F2.opExtrude","SWEPT_FACE",FACE,{"disambiguationData":[OSD([sQuery(id+"F0.wireOp",EDGE,"E6.1.0")])]}),makeQuery(id+"F6.opExtrude","SWEPT_FACE",FACE,{"disambiguationData":[OSD([sQuery(id+"F5.wireOp",EDGE,"E11.1.2")])]})]});
            var Q19;
            Q19=makeQuery(id+"F6.boolean.opBoolean","INTERSECT",EDGE,{"derivedFrom":[makeQuery(id+"F2.opExtrude","SWEPT_FACE",FACE,{"disambiguationData":[OSD([sQuery(id+"F0.wireOp",EDGE,"E6.1.0")])]}),makeQuery(id+"F6.opExtrude","SWEPT_FACE",FACE,{"disambiguationData":[OSD([sQuery(id+"F5.wireOp",EDGE,"E11.1.0")])]})]});
            chamfer(context, id + "F7", {"entities" : qUnion([Q0, Q1, Q2, Q3, Q4, Q5, Q6, Q7, Q8, Q9, Q10, Q11, Q12, Q13, Q14, Q15, Q16, Q17, Q18, Q19]), "width" : 0.76 * mm, "tangentPropagation" : true});
        }
    });
